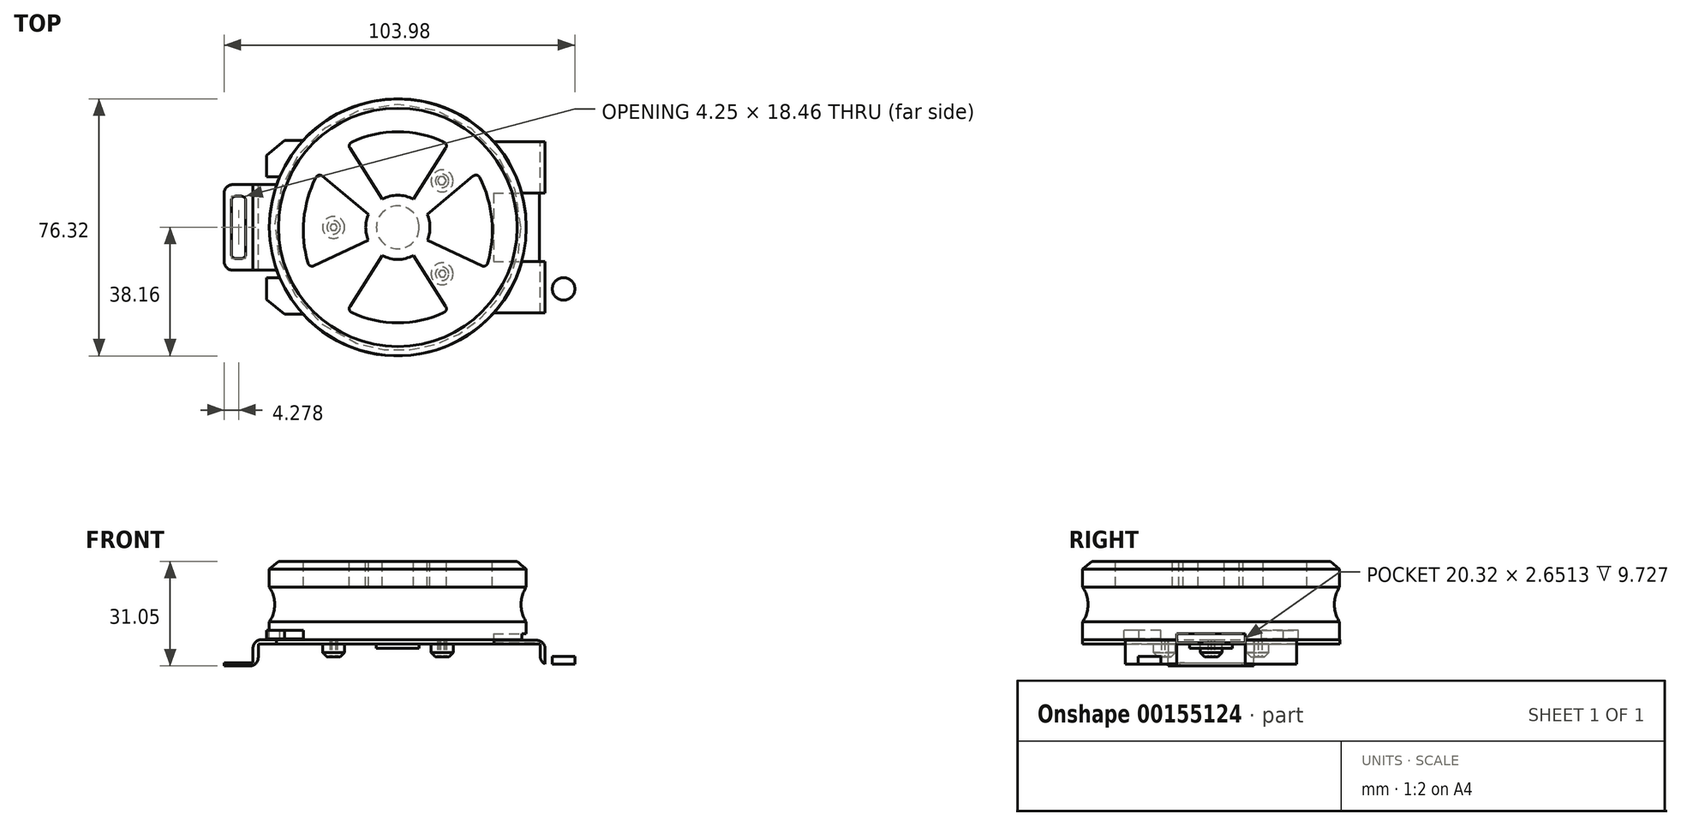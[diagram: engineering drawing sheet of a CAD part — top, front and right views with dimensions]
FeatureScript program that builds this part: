
annotation { "Feature Type Name" : "Feature", "Feature Type Description" : "" }
export const myFeature = defineFeature(function(context is Context, id is Id, definition is map)
    precondition{}
    {
        {
            var Q0;
            Q0=qCreatedBy(makeId("Front.planeOp"),FACE);
            var sketch = newSketch(context, id + "F0", { "sketchPlane" : qUnion([Q0])});
            skLineSegment(sketch, "E0", {"start": v(38.1, 10.47) * mm, "end": v(38.1, 5.16) * mm});
            skArc(sketch, "E1", {"start": v(38.1, 5.16) * mm, "mid": v(36.5, 0) * mm, "end": v(38.1, -5.16) * mm});
            skLineSegment(sketch, "E2", {"start": v(38.1, 10.47) * mm, "end": v(35.38, 12.8) * mm});
            skLineSegment(sketch, "E3", {"start": v(35.38, 12.8) * mm, "end": v(0, 12.8) * mm});
            skLineSegment(sketch, "E4", {"start": v(0, 12.8) * mm, "end": v(0, -5.16) * mm});
            skLineSegment(sketch, "E5", {"start": v(0, 25.5) * mm, "end": v(0, -17.47) * mm, "construction": true});
            skLineSegment(sketch, "E6", {"start": v(38.1, -5.16) * mm, "end": v(38.1, -10.47) * mm});
            skLineSegment(sketch, "E7", {"start": v(38.1, -10.47) * mm, "end": v(0, -10.47) * mm});
            skLineSegment(sketch, "E8", {"start": v(0, 12.8) * mm, "end": v(0, -10.47) * mm});
            skSolve(sketch);
        }
        {
            var Q0;
            Q0 = qSketchRegion(id + "F0", true);
            var Q1;
            Q1=sQuery(id+"F0.wireOp",EDGE,"E5");
            revolve(context, id + "F1", {"entities" : qUnion([Q0]), "axis" : qUnion([Q1]), "revolveType" : RevolveType.FULL});
        }
        {
            var Q0;
            Q0=makeQuery(id+"F1.opRevolve","SWEPT_FACE",FACE,{"disambiguationData":[OSD([sQuery(id+"F0.wireOp",EDGE,"E3")])]});
            var sketch = newSketch(context, id + "F2", { "sketchPlane" : qUnion([Q0])});
            skCircle(sketch, "E9", {"center": v(0, 0) * mm, "radius": 9.53 * mm});
            skLineSegment(sketch, "E10", {"start": v(-4.58, 8.35) * mm, "end": v(-14.97, 24.65) * mm});
            skLineSegment(sketch, "E11", {"start": v(4.58, 8.35) * mm, "end": v(14.97, 24.65) * mm});
            skArc(sketch, "E12", {"start": v(14.97, 24.65) * mm, "mid": v(0, 28.36) * mm, "end": v(-14.97, 24.65) * mm});
            skLineSegment(sketch, "E13.MirrorCS", {"start": v(4.58, -8.35) * mm, "end": v(14.97, -24.65) * mm});
            skLineSegment(sketch, "E14.MirrorCS", {"start": v(-4.58, -8.35) * mm, "end": v(-14.97, -24.65) * mm});
            skArc(sketch, "E15.MirrorCS", {"start": v(14.97, -24.65) * mm, "mid": v(0, -28.36) * mm, "end": v(-14.97, -24.65) * mm});
            skLineSegment(sketch, "E16", {"start": v(-8.72, 3.82) * mm, "end": v(-23.56, 16.2) * mm});
            skLineSegment(sketch, "E17", {"start": v(-8.72, -3.82) * mm, "end": v(-26.22, -12.04) * mm});
            skArc(sketch, "E18", {"start": v(-23.56, 16.2) * mm, "mid": v(-27.86, 2.36) * mm, "end": v(-26.22, -12.04) * mm});
            skLineSegment(sketch, "E19.MirrorCS", {"start": v(8.72, 3.82) * mm, "end": v(23.56, 16.2) * mm});
            skLineSegment(sketch, "E20.MirrorCS", {"start": v(8.72, -3.82) * mm, "end": v(26.22, -12.04) * mm});
            skArc(sketch, "E21.MirrorCS", {"start": v(23.56, 16.2) * mm, "mid": v(27.86, 2.36) * mm, "end": v(26.22, -12.04) * mm});
            skSolve(sketch);
        }
        {
            var Q0;
            {var subQ0=sQuery(id+"F2.wireOp",EDGE,"E10");Q0=makeQuery(id+"F2.imprint","IMPRINT",FACE,{"disambiguationData":[TD([[makeQuery(id+"F2.imprint","IMPRINT",EDGE,{"derivedFrom":subQ0}),-1.0]])]});}
            var Q1;
            {var subQ0=sQuery(id+"F2.wireOp",EDGE,"E16");Q1=makeQuery(id+"F2.imprint","IMPRINT",FACE,{"disambiguationData":[TD([[makeQuery(id+"F2.imprint","IMPRINT",EDGE,{"derivedFrom":subQ0}),1.0]])]});}
            var Q2;
            {var subQ0=sQuery(id+"F2.wireOp",EDGE,"E13.MirrorCS");Q2=makeQuery(id+"F2.imprint","IMPRINT",FACE,{"disambiguationData":[TD([[makeQuery(id+"F2.imprint","IMPRINT",EDGE,{"derivedFrom":subQ0}),-1.0]])]});}
            var Q3;
            {var subQ0=sQuery(id+"F2.wireOp",EDGE,"E19.MirrorCS");Q3=makeQuery(id+"F2.imprint","IMPRINT",FACE,{"disambiguationData":[TD([[makeQuery(id+"F2.imprint","IMPRINT",EDGE,{"derivedFrom":subQ0}),-1.0]])]});}
            extrude(context, id + "F3", {"entities" : qUnion([Q0, Q1, Q2, Q3]), "operationType" : NewBodyOperationType.REMOVE, "oppositeDirection" : true, "depth" : 7.62 * mm});
        }
        {
            var Q0;
            Q0=makeQuery(id+"F3.boolean.opBoolean","COPY",EDGE,{"derivedFrom":makeQuery(id+"F3.opExtrude","SWEPT_EDGE",EDGE,{"disambiguationData":[OSD([sQuery(id+"F2.wireOp",EDGE,"E16"),sQuery(id+"F2.wireOp",EDGE,"E18")])]})});
            var Q1;
            Q1=makeQuery(id+"F3.boolean.opBoolean","COPY",EDGE,{"derivedFrom":makeQuery(id+"F3.opExtrude","SWEPT_EDGE",EDGE,{"disambiguationData":[OSD([sQuery(id+"F2.wireOp",EDGE,"E17"),sQuery(id+"F2.wireOp",EDGE,"E18")])]})});
            fillet(context, id + "F4", {"entities" : qUnion([Q0, Q1]), "radius" : 1.27 * mm, "tangentPropagation" : true, "allowEdgeOverflow" : false});
        }
        {
            var Q0;
            Q0=makeQuery(id+"F3.boolean.opBoolean","COPY",EDGE,{"derivedFrom":makeQuery(id+"F3.opExtrude","SWEPT_EDGE",EDGE,{"disambiguationData":[OSD([sQuery(id+"F2.wireOp",EDGE,"E19.MirrorCS"),sQuery(id+"F2.wireOp",EDGE,"E21.MirrorCS")])]})});
            var Q1;
            Q1=makeQuery(id+"F3.boolean.opBoolean","COPY",EDGE,{"derivedFrom":makeQuery(id+"F3.opExtrude","SWEPT_EDGE",EDGE,{"disambiguationData":[OSD([sQuery(id+"F2.wireOp",EDGE,"E20.MirrorCS"),sQuery(id+"F2.wireOp",EDGE,"E21.MirrorCS")])]})});
            fillet(context, id + "F5", {"entities" : qUnion([Q0, Q1]), "radius" : 1.27 * mm, "tangentPropagation" : true, "allowEdgeOverflow" : false});
        }
        {
            var Q0;
            Q0=makeQuery(id+"F3.boolean.opBoolean","COPY",EDGE,{"derivedFrom":makeQuery(id+"F3.opExtrude","SWEPT_EDGE",EDGE,{"disambiguationData":[OSD([sQuery(id+"F2.wireOp",EDGE,"E11"),sQuery(id+"F2.wireOp",EDGE,"E12")])]})});
            var Q1;
            Q1=makeQuery(id+"F3.boolean.opBoolean","COPY",EDGE,{"derivedFrom":makeQuery(id+"F3.opExtrude","SWEPT_EDGE",EDGE,{"disambiguationData":[OSD([sQuery(id+"F2.wireOp",EDGE,"E10"),sQuery(id+"F2.wireOp",EDGE,"E12")])]})});
            fillet(context, id + "F6", {"entities" : qUnion([Q0, Q1]), "radius" : 1.27 * mm, "tangentPropagation" : true, "allowEdgeOverflow" : false});
        }
        {
            var Q0;
            Q0=makeQuery(id+"F3.boolean.opBoolean","COPY",EDGE,{"derivedFrom":makeQuery(id+"F3.opExtrude","SWEPT_EDGE",EDGE,{"disambiguationData":[OSD([sQuery(id+"F2.wireOp",EDGE,"E14.MirrorCS"),sQuery(id+"F2.wireOp",EDGE,"E15.MirrorCS")])]})});
            var Q1;
            Q1=makeQuery(id+"F3.boolean.opBoolean","COPY",EDGE,{"derivedFrom":makeQuery(id+"F3.opExtrude","SWEPT_EDGE",EDGE,{"disambiguationData":[OSD([sQuery(id+"F2.wireOp",EDGE,"E13.MirrorCS"),sQuery(id+"F2.wireOp",EDGE,"E15.MirrorCS")])]})});
            fillet(context, id + "F7", {"entities" : qUnion([Q0, Q1]), "radius" : 1.27 * mm, "tangentPropagation" : true, "allowEdgeOverflow" : false});
        }
        {
            var Q0;
            Q0=makeQuery(id+"F1.opRevolve","SWEPT_FACE",FACE,{"disambiguationData":[OSD([sQuery(id+"F0.wireOp",EDGE,"E7")])]});
            var sketch = newSketch(context, id + "F8", { "sketchPlane" : qUnion([Q0])});
            skCircle(sketch, "E22", {"center": v(0, 0) * mm, "radius": 6.35 * mm});
            skCircle(sketch, "E23", {"center": v(0, 0) * mm, "radius": 19.05 * mm});
            skCircle(sketch, "E24", {"center": v(0, 0) * mm, "radius": 38.16 * mm});
            skCircle(sketch, "E25", {"center": v(-19.05, 0) * mm, "radius": 3.25 * mm});
            skCircle(sketch, "E26", {"center": v(13.14, 13.79) * mm, "radius": 3.25 * mm});
            skCircle(sketch, "E27.MirrorC", {"center": v(13.14, -13.79) * mm, "radius": 3.25 * mm});
            skSolve(sketch);
        }
        {
            var Q0;
            Q0=makeQuery(id+"F8.imprint","IMPRINT",FACE,{"disambiguationData":[TD([[makeQuery(id+"F8.imprint","IMPRINT",EDGE,{"derivedFrom":sQuery(id+"F8.wireOp",EDGE,"E24")}),1.0]])]});
            var Q1;
            Q1=makeQuery(id+"F8.imprint","IMPRINT",FACE,{"disambiguationData":[TD([[makeQuery(id+"F8.imprint","IMPRINT",EDGE,{"derivedFrom":sQuery(id+"F8.wireOp",EDGE,"E22")}),1.0]])]});
            var Q2;
            Q2=makeQuery(id+"F8.imprint","IMPRINT",FACE,{"disambiguationData":[TD([[makeQuery(id+"F8.imprint","IMPRINT",EDGE,{"derivedFrom":sQuery(id+"F8.wireOp",EDGE,"E23")}),-1.0]])]});
            var Q3;
            Q3=makeQuery(id+"F8.imprint","IMPRINT",FACE,{"disambiguationData":[TD([[makeQuery(id+"F8.imprint","IMPRINT",EDGE,{"derivedFrom":sQuery(id+"F8.wireOp",EDGE,"E22")}),-1.0]])]});
            extrude(context, id + "F9", {"entities" : qUnion([Q0, Q1, Q2, Q3]), "operationType" : NewBodyOperationType.ADD, "depth" : 1.27 * mm});
        }
        {
            var Q0;
            Q0=makeQuery(id+"F9.opExtrude","CAP_FACE",FACE,{"disambiguationData":[OSD([sQuery(id+"F8.wireOp",EDGE,"E24"),sQuery(id+"F8.wireOp",EDGE,"E25"),sQuery(id+"F8.wireOp",EDGE,"E26"),sQuery(id+"F8.wireOp",EDGE,"E27.MirrorC")])],"isStart":false});
            var sketch = newSketch(context, id + "F10", { "sketchPlane" : qUnion([Q0])});
            skCircle(sketch, "E28", {"center": v(0, 0) * mm, "radius": 6.35 * mm});
            skSolve(sketch);
        }
        {
            var Q0;
            Q0 = qSketchRegion(id + "F10", true);
            extrude(context, id + "F11", {"entities" : qUnion([Q0]), "operationType" : NewBodyOperationType.ADD, "depth" : 1.27 * mm});
        }
        {
            var Q0;
            Q0=makeQuery(id+"F9.boolean.opBoolean","SPLIT",FACE,{"disambiguationData":[TD([makeQuery(id+"F9.opExtrude","SWEPT_FACE",FACE,{"disambiguationData":[OSD([sQuery(id+"F8.wireOp",EDGE,"E25")])]})])],"derivedFrom":makeQuery(id+"F1.opRevolve","SWEPT_FACE",FACE,{"disambiguationData":[OSD([sQuery(id+"F0.wireOp",EDGE,"E7")])]})});
            var Q1;
            Q1=makeQuery(id+"F9.boolean.opBoolean","SPLIT",FACE,{"disambiguationData":[TD([makeQuery(id+"F9.opExtrude","SWEPT_FACE",FACE,{"disambiguationData":[OSD([sQuery(id+"F8.wireOp",EDGE,"E26")])]})])],"derivedFrom":makeQuery(id+"F1.opRevolve","SWEPT_FACE",FACE,{"disambiguationData":[OSD([sQuery(id+"F0.wireOp",EDGE,"E7")])]})});
            var Q2;
            Q2=makeQuery(id+"F9.boolean.opBoolean","SPLIT",FACE,{"disambiguationData":[TD([makeQuery(id+"F9.opExtrude","SWEPT_FACE",FACE,{"disambiguationData":[OSD([sQuery(id+"F8.wireOp",EDGE,"E27.MirrorC")])]})])],"derivedFrom":makeQuery(id+"F1.opRevolve","SWEPT_FACE",FACE,{"disambiguationData":[OSD([sQuery(id+"F0.wireOp",EDGE,"E7")])]})});
            extrude(context, id + "F12", {"entities" : qUnion([Q0, Q1, Q2]), "operationType" : NewBodyOperationType.ADD, "depth" : 5.08 * mm});
        }
        {
            var Q0;
            Q0=makeQuery(id+"F12.opExtrude","CAP_EDGE",EDGE,{"disambiguationData":[OSD([sQuery(id+"F8.wireOp",EDGE,"E25")])],"isStart":false});
            var Q1;
            Q1=makeQuery(id+"F12.opExtrude","CAP_EDGE",EDGE,{"disambiguationData":[OSD([sQuery(id+"F8.wireOp",EDGE,"E26")])],"isStart":false});
            var Q2;
            Q2=makeQuery(id+"F12.opExtrude","CAP_EDGE",EDGE,{"disambiguationData":[OSD([sQuery(id+"F8.wireOp",EDGE,"E27.MirrorC")])],"isStart":false});
            chamfer(context, id + "F13", {"entities" : qUnion([Q0, Q1, Q2]), "width" : 1.27 * mm, "tangentPropagation" : true});
        }
        {
            var Q0;
            {var subQ0=sQuery(id+"F0.wireOp",EDGE,"E7");Q0=makeQuery(id+"F12.opExtrude","CAP_FACE",FACE,{"disambiguationData":[OSD([subQ0]),TDD([makeQuery(id+"F9.boolean.opBoolean","SPLIT",FACE,{"disambiguationData":[TD([makeQuery(id+"F9.opExtrude","SWEPT_FACE",FACE,{"disambiguationData":[OSD([sQuery(id+"F8.wireOp",EDGE,"E25")])]})])],"derivedFrom":makeQuery(id+"F1.opRevolve","SWEPT_FACE",FACE,{"disambiguationData":[OSD([subQ0])]})})])],"isStart":false});}
            var sketch = newSketch(context, id + "F14", { "sketchPlane" : qUnion([Q0])});
            skCircle(sketch, "E29.cCircle", {"center": v(-19.05, 0) * mm, "radius": 0.93 * mm, "construction": true});
            skLineSegment(sketch, "E29.0", {"start": v(-18.51, -0.93) * mm, "end": v(-19.59, -0.93) * mm});
            skLineSegment(sketch, "E29.1", {"start": v(-19.59, -0.93) * mm, "end": v(-20.13, 0) * mm});
            skLineSegment(sketch, "E29.2", {"start": v(-20.13, 0) * mm, "end": v(-19.59, 0.93) * mm});
            skLineSegment(sketch, "E29.3", {"start": v(-19.59, 0.93) * mm, "end": v(-18.51, 0.93) * mm});
            skLineSegment(sketch, "E29.4", {"start": v(-18.51, 0.93) * mm, "end": v(-17.97, 0) * mm});
            skLineSegment(sketch, "E29.5", {"start": v(-17.97, 0) * mm, "end": v(-18.51, -0.93) * mm});
            skPoint(sketch, "E29.0.midPoint", {"position": v(-19.05, -0.93) * mm});
            skCircle(sketch, "E30.cCircle", {"center": v(13.18, 13.76) * mm, "radius": 1 * mm, "construction": true});
            skLineSegment(sketch, "E30.0", {"start": v(13.76, 12.76) * mm, "end": v(12.6, 12.76) * mm});
            skLineSegment(sketch, "E30.1", {"start": v(12.6, 12.76) * mm, "end": v(12.03, 13.76) * mm});
            skLineSegment(sketch, "E30.2", {"start": v(12.03, 13.76) * mm, "end": v(12.6, 14.75) * mm});
            skLineSegment(sketch, "E30.3", {"start": v(12.6, 14.75) * mm, "end": v(13.76, 14.75) * mm});
            skLineSegment(sketch, "E30.4", {"start": v(13.76, 14.75) * mm, "end": v(14.34, 13.76) * mm});
            skLineSegment(sketch, "E30.5", {"start": v(14.34, 13.76) * mm, "end": v(13.76, 12.76) * mm});
            skPoint(sketch, "E30.0.midPoint", {"position": v(13.18, 12.76) * mm});
            skCircle(sketch, "E31.cCircle", {"center": v(13.04, -13.9) * mm, "radius": 1.16 * mm, "construction": true});
            skLineSegment(sketch, "E31.0", {"start": v(12.37, -12.74) * mm, "end": v(13.71, -12.74) * mm});
            skLineSegment(sketch, "E31.1", {"start": v(13.71, -12.74) * mm, "end": v(14.38, -13.9) * mm});
            skLineSegment(sketch, "E31.2", {"start": v(14.38, -13.9) * mm, "end": v(13.71, -15.06) * mm});
            skLineSegment(sketch, "E31.3", {"start": v(13.71, -15.06) * mm, "end": v(12.37, -15.06) * mm});
            skLineSegment(sketch, "E31.4", {"start": v(12.37, -15.06) * mm, "end": v(11.7, -13.9) * mm});
            skLineSegment(sketch, "E31.5", {"start": v(11.7, -13.9) * mm, "end": v(12.37, -12.74) * mm});
            skPoint(sketch, "E31.0.midPoint", {"position": v(13.04, -12.74) * mm});
            skSolve(sketch);
        }
        {
            var Q0;
            Q0 = qSketchRegion(id + "F14", true);
            extrude(context, id + "F15", {"entities" : qUnion([Q0]), "operationType" : NewBodyOperationType.REMOVE, "oppositeDirection" : true, "depth" : 5.08 * mm});
        }
        {
            var Q0;
            Q0=qCreatedBy(makeId("Front.planeOp"),FACE);
            var sketch = newSketch(context, id + "F16", { "sketchPlane" : qUnion([Q0])});
            skLineSegment(sketch, "E32.bottom", {"start": v(-32.21, -10.41) * mm, "end": v(-42.93, -10.41) * mm});
            skLineSegment(sketch, "E32.top", {"start": v(-32.21, -11.69) * mm, "end": v(-42.93, -11.69) * mm});
            skLineSegment(sketch, "E32.left", {"start": v(-32.21, -10.41) * mm, "end": v(-32.21, -11.69) * mm});
            skLineSegment(sketch, "E32.right", {"start": v(-42.93, -10.41) * mm, "end": v(-42.93, -11.69) * mm});
            skLineSegment(sketch, "E33.bottom", {"start": v(-42.93, -11.69) * mm, "end": v(-41.38, -11.69) * mm});
            skLineSegment(sketch, "E33.top", {"start": v(-42.93, -17.3) * mm, "end": v(-41.38, -17.3) * mm});
            skLineSegment(sketch, "E33.left", {"start": v(-42.93, -11.69) * mm, "end": v(-42.93, -17.3) * mm});
            skLineSegment(sketch, "E33.right", {"start": v(-41.38, -11.69) * mm, "end": v(-41.38, -17.3) * mm});
            skLineSegment(sketch, "E34.bottom", {"start": v(-41.38, -17.3) * mm, "end": v(-51.5, -17.3) * mm});
            skLineSegment(sketch, "E34.top", {"start": v(-41.38, -18.25) * mm, "end": v(-51.5, -18.25) * mm});
            skLineSegment(sketch, "E34.left", {"start": v(-41.38, -17.3) * mm, "end": v(-41.38, -18.25) * mm});
            skLineSegment(sketch, "E34.right", {"start": v(-51.5, -17.3) * mm, "end": v(-51.5, -18.25) * mm});
            skSolve(sketch);
        }
        {
            var Q0;
            Q0 = qSketchRegion(id + "F16", true);
            extrude(context, id + "F17", {"entities" : qUnion([Q0]), "operationType" : NewBodyOperationType.ADD, "depth" : 25.4 * mm, "symmetric" : true});
        }
        {
            var Q0;
            Q0=makeQuery(id+"F17.opExtrude","SWEPT_FACE",FACE,{"disambiguationData":[OSD([sQuery(id+"F16.wireOp",EDGE,"E34.bottom")])]});
            var sketch = newSketch(context, id + "F18", { "sketchPlane" : qUnion([Q0])});
            skLineSegment(sketch, "E35.bottom", {"start": v(-45.09, -9.23) * mm, "end": v(-49.34, -9.23) * mm});
            skLineSegment(sketch, "E35.top", {"start": v(-45.09, 9.23) * mm, "end": v(-49.34, 9.23) * mm});
            skLineSegment(sketch, "E35.left", {"start": v(-45.09, -9.23) * mm, "end": v(-45.09, 9.23) * mm});
            skLineSegment(sketch, "E35.right", {"start": v(-49.34, -9.23) * mm, "end": v(-49.34, 9.23) * mm});
            skPoint(sketch, "E35.middle", {"position": v(-47.21, 0) * mm});
            skPoint(sketch, "E35.middle.positionSnap0", {"position": v(-47.21, -12.7) * mm});
            skPoint(sketch, "E35.centerSnap0", {"position": v(-47.21, -12.7) * mm});
            skSolve(sketch);
        }
        {
            var Q0;
            Q0 = qSketchRegion(id + "F18", true);
            extrude(context, id + "F19", {"entities" : qUnion([Q0]), "operationType" : NewBodyOperationType.REMOVE, "oppositeDirection" : true, "depth" : 25.4 * mm});
        }
        {
            var Q0;
            Q0=makeQuery(id+"F19.boolean.opBoolean","COPY",EDGE,{"derivedFrom":makeQuery(id+"F19.opExtrude","SWEPT_EDGE",EDGE,{"disambiguationData":[OSD([sQuery(id+"F18.wireOp",EDGE,"E35.top"),sQuery(id+"F18.wireOp",EDGE,"E35.right")])]})});
            var Q1;
            Q1=makeQuery(id+"F19.boolean.opBoolean","COPY",EDGE,{"derivedFrom":makeQuery(id+"F19.opExtrude","SWEPT_EDGE",EDGE,{"disambiguationData":[OSD([sQuery(id+"F18.wireOp",EDGE,"E35.top"),sQuery(id+"F18.wireOp",EDGE,"E35.left")])]})});
            var Q2;
            Q2=makeQuery(id+"F19.boolean.opBoolean","COPY",EDGE,{"derivedFrom":makeQuery(id+"F19.opExtrude","SWEPT_EDGE",EDGE,{"disambiguationData":[OSD([sQuery(id+"F18.wireOp",EDGE,"E35.bottom"),sQuery(id+"F18.wireOp",EDGE,"E35.right")])]})});
            var Q3;
            Q3=makeQuery(id+"F19.boolean.opBoolean","COPY",EDGE,{"derivedFrom":makeQuery(id+"F19.opExtrude","SWEPT_EDGE",EDGE,{"disambiguationData":[OSD([sQuery(id+"F18.wireOp",EDGE,"E35.bottom"),sQuery(id+"F18.wireOp",EDGE,"E35.left")])]})});
            fillet(context, id + "F20", {"entities" : qUnion([Q0, Q1, Q2, Q3]), "radius" : 1.27 * mm, "tangentPropagation" : true, "allowEdgeOverflow" : false});
        }
        {
            var Q0;
            Q0=qCreatedBy(makeId("Front.planeOp"),FACE);
            var sketch = newSketch(context, id + "F21", { "sketchPlane" : qUnion([Q0])});
            skLineSegment(sketch, "E36.bottom", {"start": v(22.82, -10.63) * mm, "end": v(43.69, -10.63) * mm});
            skLineSegment(sketch, "E36.top", {"start": v(22.82, -11.74) * mm, "end": v(43.69, -11.74) * mm});
            skLineSegment(sketch, "E36.left", {"start": v(22.82, -10.63) * mm, "end": v(22.82, -11.74) * mm});
            skLineSegment(sketch, "E36.right", {"start": v(43.69, -10.63) * mm, "end": v(43.69, -11.74) * mm});
            skLineSegment(sketch, "E37.bottom", {"start": v(43.69, -11.74) * mm, "end": v(42.21, -11.74) * mm});
            skLineSegment(sketch, "E37.top", {"start": v(43.69, -15.38) * mm, "end": v(42.21, -15.38) * mm});
            skLineSegment(sketch, "E37.left", {"start": v(43.69, -11.74) * mm, "end": v(43.69, -15.38) * mm});
            skLineSegment(sketch, "E37.right", {"start": v(42.21, -11.74) * mm, "end": v(42.21, -15.38) * mm});
            skLineSegment(sketch, "E38.bottom", {"start": v(42.21, -15.38) * mm, "end": v(53.37, -15.38) * mm});
            skLineSegment(sketch, "E38.top", {"start": v(42.21, -17.66) * mm, "end": v(53.37, -17.66) * mm});
            skLineSegment(sketch, "E38.left", {"start": v(42.21, -15.38) * mm, "end": v(42.21, -17.66) * mm});
            skLineSegment(sketch, "E38.right", {"start": v(53.37, -15.38) * mm, "end": v(53.37, -17.66) * mm});
            skSolve(sketch);
        }
        {
            var Q0;
            Q0 = qSketchRegion(id + "F21", true);
            extrude(context, id + "F22", {"entities" : qUnion([Q0]), "operationType" : NewBodyOperationType.ADD, "depth" : 50.8 * mm, "symmetric" : true});
        }
        {
            var Q0;
            Q0=makeQuery(id+"F22.opExtrude","SWEPT_FACE",FACE,{"disambiguationData":[OSD([sQuery(id+"F21.wireOp",EDGE,"E38.bottom")])]});
            var sketch = newSketch(context, id + "F23", { "sketchPlane" : qUnion([Q0])});
            skCircle(sketch, "E39", {"center": v(49.14, 18.28) * mm, "radius": 3.35 * mm});
            skCircle(sketch, "E40.MirrorC", {"center": v(49.14, -18.28) * mm, "radius": 3.35 * mm});
            skSolve(sketch);
        }
        {
            var Q0;
            Q0=qCreatedBy(makeId("Front.planeOp"),FACE);
            var sketch = newSketch(context, id + "F24", { "sketchPlane" : qUnion([Q0])});
            skLineSegment(sketch, "E41.bottom", {"start": v(28.37, -8.7) * mm, "end": v(61.52, -8.7) * mm});
            skLineSegment(sketch, "E41.top", {"start": v(28.37, -11.36) * mm, "end": v(61.52, -11.36) * mm});
            skLineSegment(sketch, "E41.left", {"start": v(28.37, -8.7) * mm, "end": v(28.37, -11.36) * mm});
            skLineSegment(sketch, "E41.right", {"start": v(61.52, -8.7) * mm, "end": v(61.52, -11.36) * mm});
            skLineSegment(sketch, "E42.bottom", {"start": v(61.52, -11.36) * mm, "end": v(42.02, -11.36) * mm});
            skLineSegment(sketch, "E42.top", {"start": v(61.52, -24.64) * mm, "end": v(42.02, -24.64) * mm});
            skLineSegment(sketch, "E42.left", {"start": v(61.52, -11.36) * mm, "end": v(61.52, -24.64) * mm});
            skLineSegment(sketch, "E42.right", {"start": v(42.02, -11.36) * mm, "end": v(42.02, -24.64) * mm});
            skLineSegment(sketch, "E43.bottom", {"start": v(42.02, -24.64) * mm, "end": v(70.46, -24.64) * mm});
            skLineSegment(sketch, "E43.top", {"start": v(42.02, -14.96) * mm, "end": v(70.46, -14.96) * mm});
            skLineSegment(sketch, "E43.left", {"start": v(42.02, -24.64) * mm, "end": v(42.02, -14.96) * mm});
            skLineSegment(sketch, "E43.right", {"start": v(70.46, -24.64) * mm, "end": v(70.46, -14.96) * mm});
            skSolve(sketch);
        }
        {
            var Q0;
            Q0 = qSketchRegion(id + "F24", true);
            extrude(context, id + "F25", {"entities" : qUnion([Q0]), "operationType" : NewBodyOperationType.REMOVE, "oppositeDirection" : true, "depth" : 20.32 * mm, "symmetric" : true});
        }
        {
            var Q0;
            Q0=makeQuery(id+"F23.imprint","IMPRINT",FACE,{"disambiguationData":[TD([[makeQuery(id+"F23.imprint","IMPRINT",EDGE,{"derivedFrom":sQuery(id+"F23.wireOp",EDGE,"E39")}),1.0]])]});
            var Q1;
            Q1=makeQuery(id+"F23.imprint","IMPRINT",FACE,{"disambiguationData":[TD([[makeQuery(id+"F23.imprint","IMPRINT",EDGE,{"derivedFrom":sQuery(id+"F23.wireOp",EDGE,"E40.MirrorC")}),-1.0]])]});
            extrude(context, id + "F26", {"entities" : qUnion([Q0, Q1]), "operationType" : NewBodyOperationType.REMOVE, "oppositeDirection" : true, "depth" : 25.4 * mm});
        }
        {
            var Q0;
            {var subQ0=sQuery(id+"F21.wireOp",EDGE,"E36.bottom");var subQ1=sQuery(id+"F21.wireOp",EDGE,"E37.left");var subQ2=sQuery(id+"F21.wireOp",EDGE,"E36.right");Q0=makeQuery(id+"F25.boolean.opBoolean","SPLIT",EDGE,{"disambiguationData":[TD([makeQuery(id+"F22.opExtrude","CAP_FACE",FACE,{"disambiguationData":[OSD([subQ0,sQuery(id+"F21.wireOp",EDGE,"E36.top"),sQuery(id+"F21.wireOp",EDGE,"E36.left"),subQ2,subQ1,sQuery(id+"F21.wireOp",EDGE,"E37.right"),sQuery(id+"F21.wireOp",EDGE,"E38.bottom"),sQuery(id+"F21.wireOp",EDGE,"E38.top"),sQuery(id+"F21.wireOp",EDGE,"E38.left"),sQuery(id+"F21.wireOp",EDGE,"E38.right")])],"isStart":true})])],"derivedFrom":makeQuery(id+"F22.opExtrude","SWEPT_EDGE",EDGE,{"disambiguationData":[OSD([subQ0,subQ2])]})});}
            var Q1;
            {var subQ0=sQuery(id+"F21.wireOp",EDGE,"E38.left");var subQ1=sQuery(id+"F21.wireOp",EDGE,"E38.top");var subQ2=sQuery(id+"F21.wireOp",EDGE,"E37.right");Q1=makeQuery(id+"F25.boolean.opBoolean","SPLIT",EDGE,{"disambiguationData":[TD([makeQuery(id+"F22.opExtrude","CAP_FACE",FACE,{"disambiguationData":[OSD([sQuery(id+"F21.wireOp",EDGE,"E36.bottom"),sQuery(id+"F21.wireOp",EDGE,"E36.top"),sQuery(id+"F21.wireOp",EDGE,"E36.left"),sQuery(id+"F21.wireOp",EDGE,"E36.right"),sQuery(id+"F21.wireOp",EDGE,"E37.left"),subQ2,sQuery(id+"F21.wireOp",EDGE,"E38.bottom"),subQ1,subQ0,sQuery(id+"F21.wireOp",EDGE,"E38.right")])],"isStart":true})])],"derivedFrom":makeQuery(id+"F22.opExtrude","SWEPT_EDGE",EDGE,{"disambiguationData":[OSD([subQ1,subQ0])]})});}
            var Q2;
            {var subQ0=sQuery(id+"F21.wireOp",EDGE,"E38.left");var subQ1=sQuery(id+"F21.wireOp",EDGE,"E38.top");var subQ2=sQuery(id+"F21.wireOp",EDGE,"E37.right");Q2=makeQuery(id+"F25.boolean.opBoolean","SPLIT",EDGE,{"disambiguationData":[TD([makeQuery(id+"F22.opExtrude","CAP_FACE",FACE,{"disambiguationData":[OSD([sQuery(id+"F21.wireOp",EDGE,"E36.bottom"),sQuery(id+"F21.wireOp",EDGE,"E36.top"),sQuery(id+"F21.wireOp",EDGE,"E36.left"),sQuery(id+"F21.wireOp",EDGE,"E36.right"),sQuery(id+"F21.wireOp",EDGE,"E37.left"),subQ2,sQuery(id+"F21.wireOp",EDGE,"E38.bottom"),subQ1,subQ0,sQuery(id+"F21.wireOp",EDGE,"E38.right")])],"isStart":false})])],"derivedFrom":makeQuery(id+"F22.opExtrude","SWEPT_EDGE",EDGE,{"disambiguationData":[OSD([subQ1,subQ0])]})});}
            var Q3;
            {var subQ0=sQuery(id+"F21.wireOp",EDGE,"E36.bottom");var subQ1=sQuery(id+"F21.wireOp",EDGE,"E37.left");var subQ2=sQuery(id+"F21.wireOp",EDGE,"E36.right");Q3=makeQuery(id+"F25.boolean.opBoolean","SPLIT",EDGE,{"disambiguationData":[TD([makeQuery(id+"F22.opExtrude","CAP_FACE",FACE,{"disambiguationData":[OSD([subQ0,sQuery(id+"F21.wireOp",EDGE,"E36.top"),sQuery(id+"F21.wireOp",EDGE,"E36.left"),subQ2,subQ1,sQuery(id+"F21.wireOp",EDGE,"E37.right"),sQuery(id+"F21.wireOp",EDGE,"E38.bottom"),sQuery(id+"F21.wireOp",EDGE,"E38.top"),sQuery(id+"F21.wireOp",EDGE,"E38.left"),sQuery(id+"F21.wireOp",EDGE,"E38.right")])],"isStart":false})])],"derivedFrom":makeQuery(id+"F22.opExtrude","SWEPT_EDGE",EDGE,{"disambiguationData":[OSD([subQ0,subQ2])]})});}
            var Q4;
            Q4=makeQuery(id+"F22.opExtrude","CAP_EDGE",EDGE,{"disambiguationData":[OSD([sQuery(id+"F21.wireOp",EDGE,"E38.right")])],"isStart":false});
            var Q5;
            Q5=makeQuery(id+"F25.boolean.opBoolean","INTERSECT",EDGE,{"derivedFrom":[makeQuery(id+"F22.opExtrude","SWEPT_FACE",FACE,{"disambiguationData":[OSD([sQuery(id+"F21.wireOp",EDGE,"E38.right")])]}),makeQuery(id+"F25.opExtrude","CAP_FACE",FACE,{"disambiguationData":[OSD([sQuery(id+"F24.wireOp",EDGE,"E41.bottom"),sQuery(id+"F24.wireOp",EDGE,"E41.top"),sQuery(id+"F24.wireOp",EDGE,"E41.left"),sQuery(id+"F24.wireOp",EDGE,"E41.right"),sQuery(id+"F24.wireOp",EDGE,"E42.left"),sQuery(id+"F24.wireOp",EDGE,"E42.right"),sQuery(id+"F24.wireOp",EDGE,"E43.bottom"),sQuery(id+"F24.wireOp",EDGE,"E43.top"),sQuery(id+"F24.wireOp",EDGE,"E43.left"),sQuery(id+"F24.wireOp",EDGE,"E43.right")])],"isStart":true})]});
            var Q6;
            Q6=makeQuery(id+"F25.boolean.opBoolean","INTERSECT",EDGE,{"derivedFrom":[makeQuery(id+"F22.opExtrude","SWEPT_FACE",FACE,{"disambiguationData":[OSD([sQuery(id+"F21.wireOp",EDGE,"E38.right")])]}),makeQuery(id+"F25.opExtrude","CAP_FACE",FACE,{"disambiguationData":[OSD([sQuery(id+"F24.wireOp",EDGE,"E41.bottom"),sQuery(id+"F24.wireOp",EDGE,"E41.top"),sQuery(id+"F24.wireOp",EDGE,"E41.left"),sQuery(id+"F24.wireOp",EDGE,"E41.right"),sQuery(id+"F24.wireOp",EDGE,"E42.left"),sQuery(id+"F24.wireOp",EDGE,"E42.right"),sQuery(id+"F24.wireOp",EDGE,"E43.bottom"),sQuery(id+"F24.wireOp",EDGE,"E43.top"),sQuery(id+"F24.wireOp",EDGE,"E43.left"),sQuery(id+"F24.wireOp",EDGE,"E43.right")])],"isStart":false})]});
            var Q7;
            Q7=makeQuery(id+"F22.opExtrude","CAP_EDGE",EDGE,{"disambiguationData":[OSD([sQuery(id+"F21.wireOp",EDGE,"E38.right")])],"isStart":true});
            var Q8;
            Q8=makeQuery(id+"F17.opExtrude","SWEPT_EDGE",EDGE,{"disambiguationData":[OSD([sQuery(id+"F16.wireOp",EDGE,"E32.bottom"),sQuery(id+"F16.wireOp",EDGE,"E32.right")])]});
            var Q9;
            Q9=makeQuery(id+"F17.opExtrude","SWEPT_EDGE",EDGE,{"disambiguationData":[OSD([sQuery(id+"F16.wireOp",EDGE,"E34.top"),sQuery(id+"F16.wireOp",EDGE,"E34.left")])]});
            var Q10;
            Q10=makeQuery(id+"F17.opExtrude","CAP_EDGE",EDGE,{"disambiguationData":[OSD([sQuery(id+"F16.wireOp",EDGE,"E34.right")])],"isStart":false});
            var Q11;
            Q11=makeQuery(id+"F17.opExtrude","CAP_EDGE",EDGE,{"disambiguationData":[OSD([sQuery(id+"F16.wireOp",EDGE,"E34.right")])],"isStart":true});
            fillet(context, id + "F27", {"entities" : qUnion([Q0, Q1, Q2, Q3, Q4, Q5, Q6, Q7, Q8, Q9, Q10, Q11]), "radius" : 2.54 * mm, "tangentPropagation" : true, "allowEdgeOverflow" : false});
        }
        {
            var Q0;
            Q0=qCreatedBy(makeId("Top.planeOp"),FACE);
            var sketch = newSketch(context, id + "F28", { "sketchPlane" : qUnion([Q0])});
            skLineSegment(sketch, "E44", {"start": v(-31.75, 14.97) * mm, "end": v(-38.97, 14.97) * mm});
            skLineSegment(sketch, "E45", {"start": v(-38.97, 21.41) * mm, "end": v(-33.55, 25.8) * mm});
            skLineSegment(sketch, "E46", {"start": v(-33.55, 25.8) * mm, "end": v(-26.2, 25.8) * mm});
            skLineSegment(sketch, "E47", {"start": v(-38.97, 14.97) * mm, "end": v(-38.97, 21.41) * mm});
            skLineSegment(sketch, "E48", {"start": v(-31.75, 14.97) * mm, "end": v(-26.2, 25.8) * mm});
            skLineSegment(sketch, "E49.MirrorCS", {"start": v(-31.75, -14.97) * mm, "end": v(-38.97, -14.97) * mm});
            skLineSegment(sketch, "E50.MirrorCS", {"start": v(-38.97, -21.41) * mm, "end": v(-33.55, -25.8) * mm});
            skLineSegment(sketch, "E51.MirrorCS", {"start": v(-38.97, -14.97) * mm, "end": v(-38.97, -21.41) * mm});
            skLineSegment(sketch, "E52.MirrorCS", {"start": v(-31.75, -14.97) * mm, "end": v(-26.2, -25.8) * mm});
            skLineSegment(sketch, "E53.MirrorCS", {"start": v(-33.55, -25.8) * mm, "end": v(-26.2, -25.8) * mm});
            skSolve(sketch);
        }
        {
            var Q0;
            Q0=makeQuery(id+"F28.imprint","IMPRINT",FACE,{"disambiguationData":[TD([[makeQuery(id+"F28.imprint","IMPRINT",EDGE,{"derivedFrom":sQuery(id+"F28.wireOp",EDGE,"E44")}),-1.0]])]});
            var Q1;
            Q1=makeQuery(id+"F28.imprint","IMPRINT",FACE,{"disambiguationData":[TD([[makeQuery(id+"F28.imprint","IMPRINT",EDGE,{"derivedFrom":sQuery(id+"F28.wireOp",EDGE,"E49.MirrorCS")}),1.0]])]});
            extrude(context, id + "F29", {"entities" : qUnion([Q0, Q1]), "operationType" : NewBodyOperationType.ADD, "oppositeDirection" : true, "depth" : 10.16 * mm, "hasSecondDirection" : true, "secondDirectionOppositeDirection" : true, "secondDirectionDepth" : 7.62 * mm});
        }
    });
